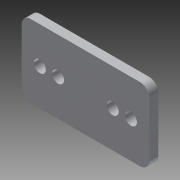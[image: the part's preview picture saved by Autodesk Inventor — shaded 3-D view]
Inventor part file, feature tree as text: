
AUTODESK INVENTOR PART (.ipt)
format: ipt  version: 2014 (Build 180170000, 170)  size: 97,280 bytes
history: native  units: in
note: dims shown in document units (in); Inventor stores cm internally (conversion verified against a paired STEP export)
features: extrude x1, sketch x1
ambient origin geometry x8: Origin, YZ Plane, XZ Plane, XY Plane, X Axis, Y Axis, Z Axis, Center Point
bodies: Solid1 (feature_tree)
feature tree (2):
  extrude  "Extrusion1"  Depth=1.0in
  sketch  "Sketch1"  dims[d0=1.75in d1=1.0in d2=0.163in d3=0.25in d5=0.7874in d7=1.0in d8=0.3937in d10=1.0in d12=0.25in d13=0.7874in d15=1.0in d16=0.3937in d18=1.0in d20=0.125in d21=0.125in d22=0.0in]
